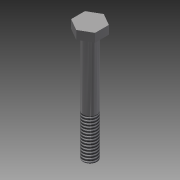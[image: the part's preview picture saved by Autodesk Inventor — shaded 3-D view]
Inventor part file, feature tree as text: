
AUTODESK INVENTOR PART (.ipt)
format: ipt  version: 2015 SP1 (Build 190203100, 203)  size: 109,056 bytes
history: native  units: in
note: dims shown in document units (in); Inventor stores cm internally (conversion verified against a paired STEP export)
features: extrude x2, sketch x2, thread x1
ambient origin geometry x8: Origin, YZ Plane, XZ Plane, XY Plane, X Axis, Y Axis, Z Axis, Center Point
bodies: Solid1 (feature_tree)
feature tree (5):
  extrude  "Extrusion1"  Depth=2.0in TaperAngle=0.0deg
  extrude  "Extrusion2"  Depth=0.4375in
  thread  "Thread1"  [1 undecoded]
  sketch  "Sketch1"  dims[d0=0.25in d1=2.0in d2=0.0in]
  sketch  "Sketch2"  dims[d3=0.4375in d4=0.4375in d5=0.4375in d6=120.0deg d7=120.0deg d8=0.2188in d9=0.2188in d10=0.2188in d11=0.1562in d12=0.0in d13=0.75in d14=1.25in]
note: 1 required parameter value undecoded (feature->parameter linkage not recoverable at this tier; creation-order binding heuristic only, values carry confidence <= 0.55)
